# Revit family: Cup_Filler-Push_Button-Whitehall-BestCare-WHBF3
name_source: partatom
category: Plumbing Fixtures
units: mm (PartAtom-declared; Revit-internal decimal feet)

## family parameters
Cut with Voids When Loaded = No
Host = Face
OmniClass Number = 23.65.70.14.11
OmniClass Title = Drinking Fountains/Coolers
Part Type = Normal
Room Calculation Point = No
Round Connector Dimension = Use Diameter
Shared = Yes

## types (1)
- WHBF3
    -CG1 Custom Graphics = No
    -WF1 1500 gallon capacity, NSF 42+53, = No
    ADA Compliant = Yes
    Assembly Code = D2010800
    CW Connection = Yes
    CWFU = 1.5
    Cold Water Connection Diameter = 3/8"
    Cold Water Connection Height = 21 5/8"
    Cold Water Connection Width = 2 5/8"
    Default Elevation = 23 1/8"
    Description = BestCare® Ligature-Resistant Semi-Recessed Push Button Cup Filler
    Fill Rate = 1.0 GPM (3.8 LPM)
    Finish = Stainless Steel-Whitehall-EG10 Powder Coated White
    HW Connection = No
    HWFU = 1.5
    Height = 28 1/8"
    IAPMO Compliance = Unit is certified to ANSI A117.1, Public Law 111-380 (NO-LEAD), CHSC 116875 and NSF/ANSI 61, Section 9.
    Installation Type = Recessed Wall Mounted
    Length = 18 1/4"
    Manufacturer = Whitehall Manufacturing
    Material = Stainless Steel-Whitehall-EG10 Powder Coated White
    Model = WHBF3
    Product Documentation Link = https://www.whitehallmfg.com
    Product Page URL = https://www.whitehallmfg.com
    URL = http://www.whitehallmfg.com
    Vent Connection = No
    WFU = 2
    Waste Connection = Yes
    Waste Connection Height = 28 1/2"
    Water Connection Diameter = 1 1/4"
    Width = 18 1/4"

## geometry (parser evidence)
native form markers: Sweep x3
no freeform markers — native parametric forms only
